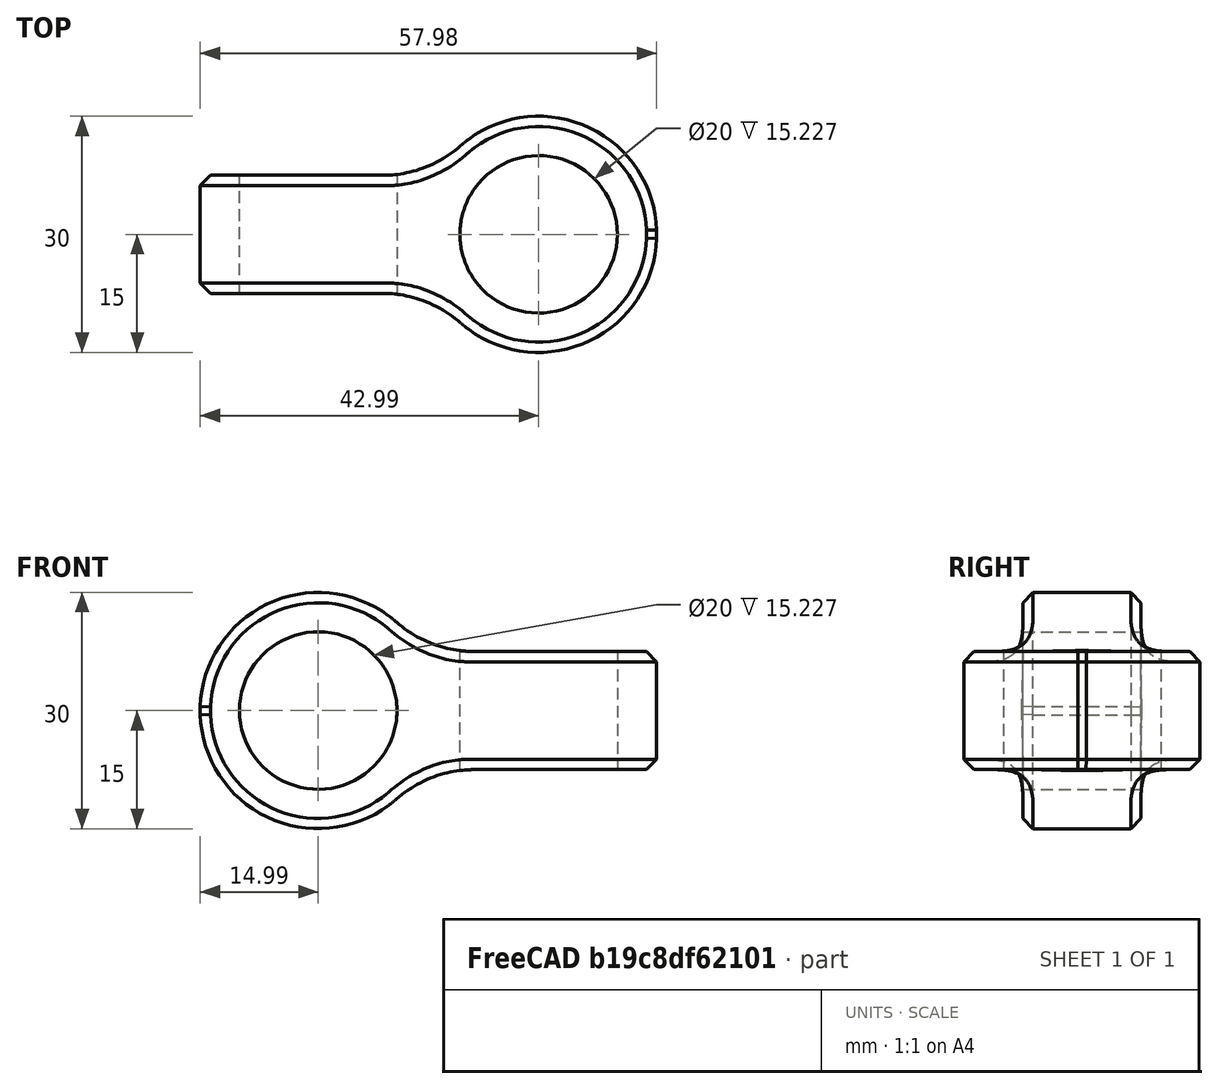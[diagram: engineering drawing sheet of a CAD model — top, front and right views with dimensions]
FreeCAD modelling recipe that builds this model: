
FCSTD DOCUMENT  (FreeCAD 0.21R33771 (Git))
Label: item_03
License: All rights reserved
LicenseURL: http://en.wikipedia.org/wiki/All_rights_reserved
objects: TechDraw::DrawViewDimension×4, TechDraw::DrawProjGroupItem×3, PartDesign::Body×2, Sketcher::SketchObject×1, PartDesign::Pad×1, PartDesign::Fillet×1, PartDesign::FeatureBase×1, Part::MultiCommon×1, Part::Chamfer×1, TechDraw::DrawSVGTemplate×1, TechDraw::DrawViewPart×1, TechDraw::DrawProjGroup×1, TechDraw::DrawViewAnnotation×1, TechDraw::DrawPage×1
note: 16 computed .brp shape members not serialized (recipe doc carries the construction recipe); baked Part::Feature solids carry a one-line shape summary decoded from their .brp

FEATURE [Sketcher::SketchObject] Sketch
  FullyConstrained = true
  MapMode = 5
  Placement = pos=(0,0,0) rot=(1,0,0;1.5708rad)
  Support = -> [XZ_Plane]
  sketch-geometry (6):
    g0: LineSegment StartX=12.9904 StartY=7.5 StartZ=0 EndX=42.9904 EndY=7.5 EndZ=0
    g1: LineSegment StartX=42.9904 StartY=7.5 StartZ=0 EndX=42.9904 EndY=-7.5 EndZ=0
    g2: LineSegment StartX=42.9904 StartY=-7.5 StartZ=0 EndX=12.9904 EndY=-7.5 EndZ=0
    g3: GeomPoint X=0 Y=0 Z=0
    g4: ArcOfCircle CenterX=0 CenterY=0 CenterZ=0 NormalX=0 NormalY=0 NormalZ=1 AngleXU=0 Radius=15 StartAngle=0.523599 EndAngle=5.75959
    g5: Circle CenterX=0 CenterY=0 CenterZ=0 NormalX=0 NormalY=0 NormalZ=1 AngleXU=0 Radius=10
  constraints (15):
    c: Coincident(g0,g1)
    c: Coincident(g1,g2)
    c: Horizontal(g0)
    c: Horizontal(g2)
    c: Coincident(g3,g-1)
    c: PointOnObject(g4,g-1)
    c: PointOnObject(g4,g-2)
    c: Symmetric(g0,g1,g-1)
    c: Diameter(g4) = 30
    c: DistanceY(g1,g1) = 15
    c: Coincident(g4,g2)
    c: Coincident(g4,g0)
    c: Coincident(g5,g4)
    c: Diameter(g5) = 20
    c: DistanceX(g0,g0) = 30
FEATURE [PartDesign::Pad] Pad
  Direction = (0,-1,2e-16)
  Length = 40
  Length2 = 10
  Midplane = true
  Placement = pos=(0,0,0) rot=(1,0,0;1.5708rad)
  Profile = -> Sketch
  ReferenceAxis = -> Sketch [N_Axis]
  Type = 0
FEATURE [PartDesign::Fillet] Fillet
  Base = -> Pad [Edge1,Edge8]
  BaseFeature = -> Pad
  Placement = pos=(0,0,0) rot=(1,0,0;1.5708rad)
  Radius = 15
  SupportTransform = false
  UseAllEdges = false
FEATURE [PartDesign::Body] Body  label="part1"
  Group = -> [Sketch,Pad,Fillet]
  Origin = -> Origin
  Tip = -> Fillet
FEATURE [PartDesign::FeatureBase] Clone
  BaseFeature = -> Body
FEATURE [PartDesign::Body] Body001  label="part1clone1"
  Group = -> [Clone]
  Origin = -> Origin001
  Placement = pos=(28,0,3e-15) rot=(0,0.707107,-0.707107;3.14159rad)
  Tip = -> Clone
FEATURE [Part::MultiCommon] Common
  Shapes = -> [Body,Body001]
FEATURE [Part::Chamfer] Chamfer
  Base = -> Common
  Edges = 1 edges r=1.3: [Edge46]
FEATURE [TechDraw::DrawSVGTemplate] Template
  EditableTexts = Designed_by_Name=Reza Heshmati; Drawing_number=item_03; FC-Date=Date; FC-SC=Scale; FC-SH=Sheet; FC-Title=Item #3; Subtitle=Subtitle; Weight=Weight
  Height = 210
  Orientation = 1
  Template = <path>
  Width = 297
FEATURE [TechDraw::DrawViewPart] View
  Caption = 3D View
  CoarseView = false
  Direction = (0.57735,-0.57735,0.57735)
  Focus = 100
  HardHidden = false
  IsoCount = 0
  IsoHidden = false
  IsoVisible = false
  LockPosition = false
  Perspective = false
  Rotation = 0
  Scale = 2
  ScaleType = 2
  ScrubCount = 0
  SeamHidden = false
  SeamVisible = false
  SmoothHidden = false
  SmoothVisible = true
  Source = -> [Chamfer]
  X = 76.4121
  XDirection = (0.707107,0.707107,0)
  Y = 92.7355
FEATURE [TechDraw::DrawProjGroupItem] ProjItem  label="Front"
  Caption = Top View
  CoarseView = false
  Direction = (0,0,1)
  Focus = 100
  HardHidden = false
  IsoCount = 0
  IsoHidden = false
  IsoVisible = false
  LockPosition = true
  Perspective = false
  Rotation = 0
  RotationVector = (1,0,0)
  ScaleType = 2
  ScrubCount = 0
  SeamHidden = false
  SeamVisible = false
  SmoothHidden = false
  SmoothVisible = true
  Source = -> [Chamfer]
  Type = 0
  X = 0
  XDirection = (1,0,0)
  Y = 0
FEATURE [TechDraw::DrawProjGroupItem] ProjItem001  label="Right"
  Caption = Front View
  CoarseView = false
  Direction = (1,0,1e-16)
  Focus = 100
  HardHidden = false
  IsoCount = 0
  IsoHidden = false
  IsoVisible = false
  LockPosition = false
  Perspective = false
  Rotation = 0
  RotationVector = (1,0,0)
  ScaleType = 2
  ScrubCount = 0
  SeamHidden = false
  SeamVisible = false
  SmoothHidden = false
  SmoothVisible = true
  Source = -> [Chamfer]
  Type = 2
  X = -62.1774
  XDirection = (1e-16,0,-1)
  Y = 0
FEATURE [TechDraw::DrawProjGroupItem] ProjItem002  label="Bottom"
  Caption = Side View
  CoarseView = false
  Direction = (0,-1,0)
  Focus = 100
  HardHidden = false
  IsoCount = 0
  IsoHidden = false
  IsoVisible = false
  LockPosition = false
  Perspective = false
  Rotation = 0
  RotationVector = (1,0,0)
  ScaleType = 2
  ScrubCount = 0
  SeamHidden = false
  SeamVisible = false
  SmoothHidden = false
  SmoothVisible = true
  Source = -> [Chamfer]
  Type = 5
  X = 0
  XDirection = (1,0,0)
  Y = 65.2494
FEATURE [TechDraw::DrawProjGroup] ProjGroup
  Anchor = -> ProjItem
  AutoDistribute = false
  LockPosition = false
  ProjectionType = 0
  Rotation = 0
  ScaleType = 0
  Source = -> [Chamfer]
  Views = -> [ProjItem,ProjItem001,ProjItem002]
  X = 225.178
  Y = 105.18
  spacingX = 15
  spacingY = 15
FEATURE [TechDraw::DrawViewDimension] Dimension
  AngleOverride = false
  Arbitrary = false
  ArbitraryTolerances = false
  EqualTolerance = true
  ExtensionAngle = 0
  FormatSpec = ⌀%.2w
  FormatSpecOverTolerance = %+.2w
  FormatSpecUnderTolerance = %+.2w
  Inverted = false
  LineAngle = 0
  LockPosition = false
  MeasureType = 1
  OverTolerance = 0
  References2D = -> [ProjItem002]
  Rotation = 0
  ScaleType = 0
  TheoreticalExact = false
  Type = 5
  UnderTolerance = 0
  X = -45.3538
  Y = 13.8054
FEATURE [TechDraw::DrawViewDimension] Dimension001
  AngleOverride = false
  Arbitrary = false
  ArbitraryTolerances = false
  EqualTolerance = true
  ExtensionAngle = 0
  FormatSpec = ⌀%.2w
  FormatSpecOverTolerance = %+.2w
  FormatSpecUnderTolerance = %+.2w
  Inverted = false
  LineAngle = 0
  LockPosition = false
  MeasureType = 1
  OverTolerance = 0
  References2D = -> [ProjItem]
  Rotation = 0
  ScaleType = 0
  TheoreticalExact = false
  Type = 5
  UnderTolerance = 0
  X = 31.7693
  Y = 28.8999
FEATURE [TechDraw::DrawViewDimension] Dimension002
  AngleOverride = false
  Arbitrary = false
  ArbitraryTolerances = false
  EqualTolerance = true
  ExtensionAngle = 0
  FormatSpec = %.2w
  FormatSpecOverTolerance = %+.2w
  FormatSpecUnderTolerance = %+.2w
  Inverted = false
  LineAngle = 0
  LockPosition = false
  MeasureType = 1
  OverTolerance = 0
  References2D = -> [ProjItem001]
  Rotation = 0
  ScaleType = 0
  TheoreticalExact = false
  Type = 1
  UnderTolerance = 0
  X = -0.38611
  Y = 31.7558
FEATURE [TechDraw::DrawViewDimension] Dimension003
  AngleOverride = false
  Arbitrary = false
  ArbitraryTolerances = false
  EqualTolerance = true
  ExtensionAngle = 0
  FormatSpec = %.2w
  FormatSpecOverTolerance = %+.2w
  FormatSpecUnderTolerance = %+.2w
  Inverted = false
  LineAngle = 0
  LockPosition = false
  MeasureType = 1
  OverTolerance = 0
  References2D = -> [ProjItem001]
  Rotation = 0
  ScaleType = 0
  TheoreticalExact = false
  Type = 2
  UnderTolerance = 0
  X = -23.8967
  Y = 2.7011
FEATURE [TechDraw::DrawViewAnnotation] Annotation
  Caption = Extra Information
  Font = osifont
  LineSpace = 100
  LockPosition = false
  MaxWidth = -1
  Rotation = 0
  ScaleType = 0
  Text = Fillet = 15 | Chamfer = 1.3
  TextSize = 5
  TextStyle = 0
  X = 45.6982
  Y = 179.995
FEATURE [TechDraw::DrawPage] Page
  KeepUpdated = true
  NextBalloonIndex = 1
  ProjectionType = 0
  Template = -> Template
  Views = -> [View,ProjGroup,Dimension,Dimension001,Dimension002,Dimension003,Annotation]
note: 1 file-system path scrubbed to <path> (originals preserved in the JSON sidecar)
